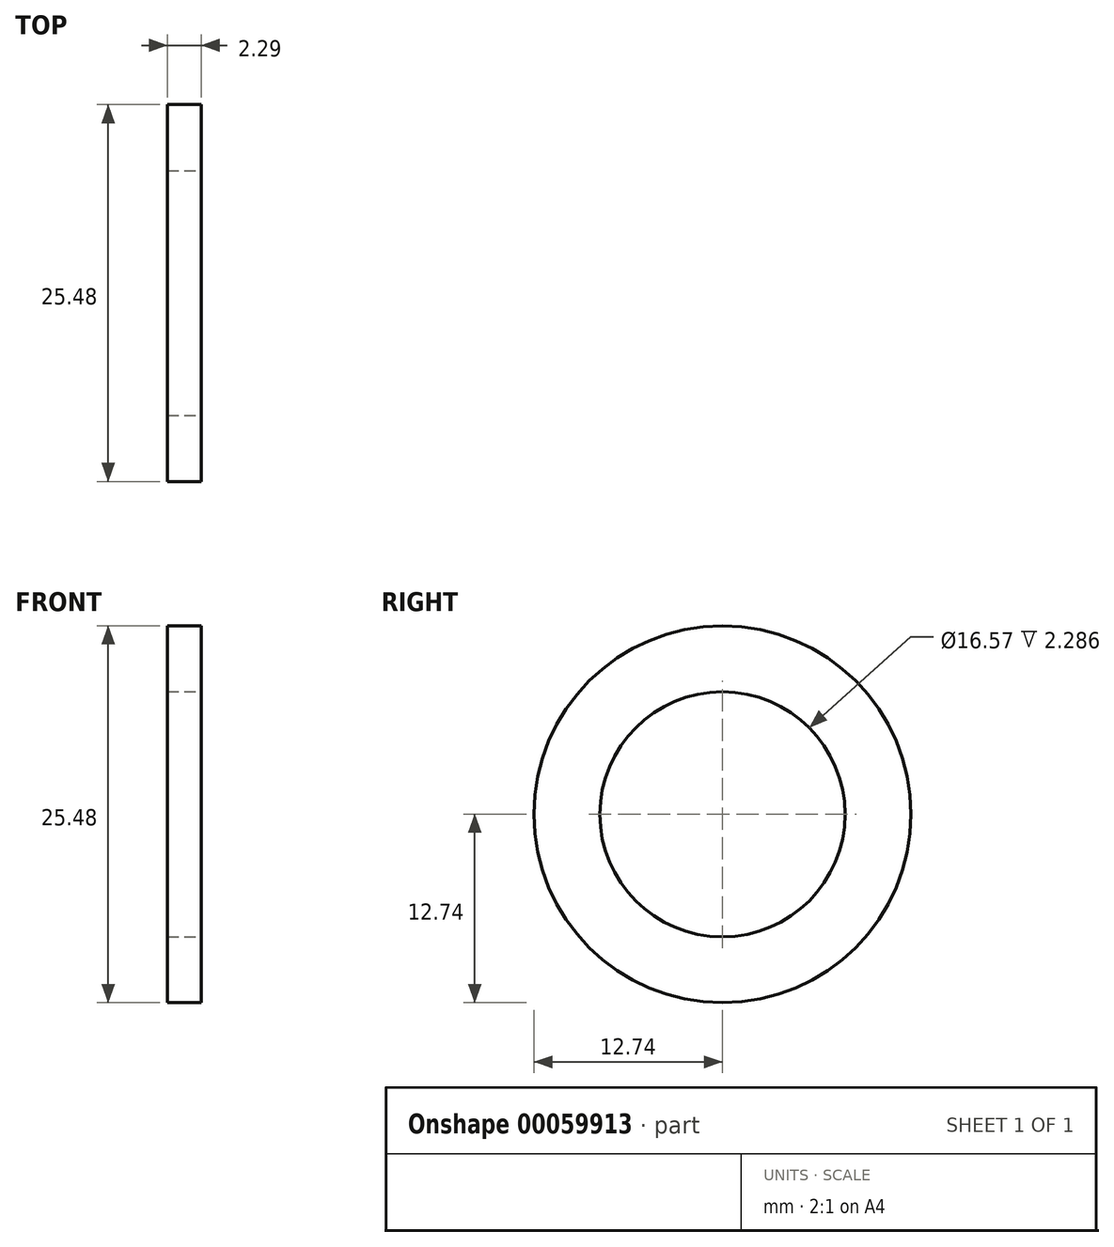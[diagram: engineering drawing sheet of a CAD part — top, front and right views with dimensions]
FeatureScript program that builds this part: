
annotation { "Feature Type Name" : "Feature", "Feature Type Description" : "" }
export const myFeature = defineFeature(function(context is Context, id is Id, definition is map)
    precondition{}
    {
        {
            var Q0;
            Q0=qCreatedBy(makeId("Right.planeOp"),FACE);
            var sketch = newSketch(context, id + "F0", { "sketchPlane" : qUnion([Q0])});
            skCircle(sketch, "E0", {"center": v(0, 0) * mm, "radius": 12.74 * mm});
            skSolve(sketch);
        }
        {
            var Q0;
            Q0=makeQuery(id+"F0.imprint","IMPRINT",FACE,{"disambiguationData":[TD([[makeQuery(id+"F0.imprint","IMPRINT",EDGE,{"derivedFrom":sQuery(id+"F0.wireOp",EDGE,"E0")}),1.0]])]});
            extrude(context, id + "F1", {"entities" : qUnion([Q0]), "depth" : 2.3 * mm});
        }
        {
            var Q0;
            Q0=makeQuery(id+"F1.opExtrude","CAP_FACE",FACE,{"disambiguationData":[OSD([sQuery(id+"F0.wireOp",EDGE,"E0")])],"isStart":false});
            var sketch = newSketch(context, id + "F2", { "sketchPlane" : qUnion([Q0])});
            skCircle(sketch, "E1", {"center": v(0, 0) * mm, "radius": 8.28 * mm});
            skSolve(sketch);
        }
        {
            var Q0;
            Q0 = qSketchRegion(id + "F2", true);
            extrude(context, id + "F3", {"entities" : qUnion([Q0]), "operationType" : NewBodyOperationType.REMOVE, "endBound" : BoundingType.SYMMETRIC, "oppositeDirection" : true, "depth" : 25.4 * mm});
        }
    });
